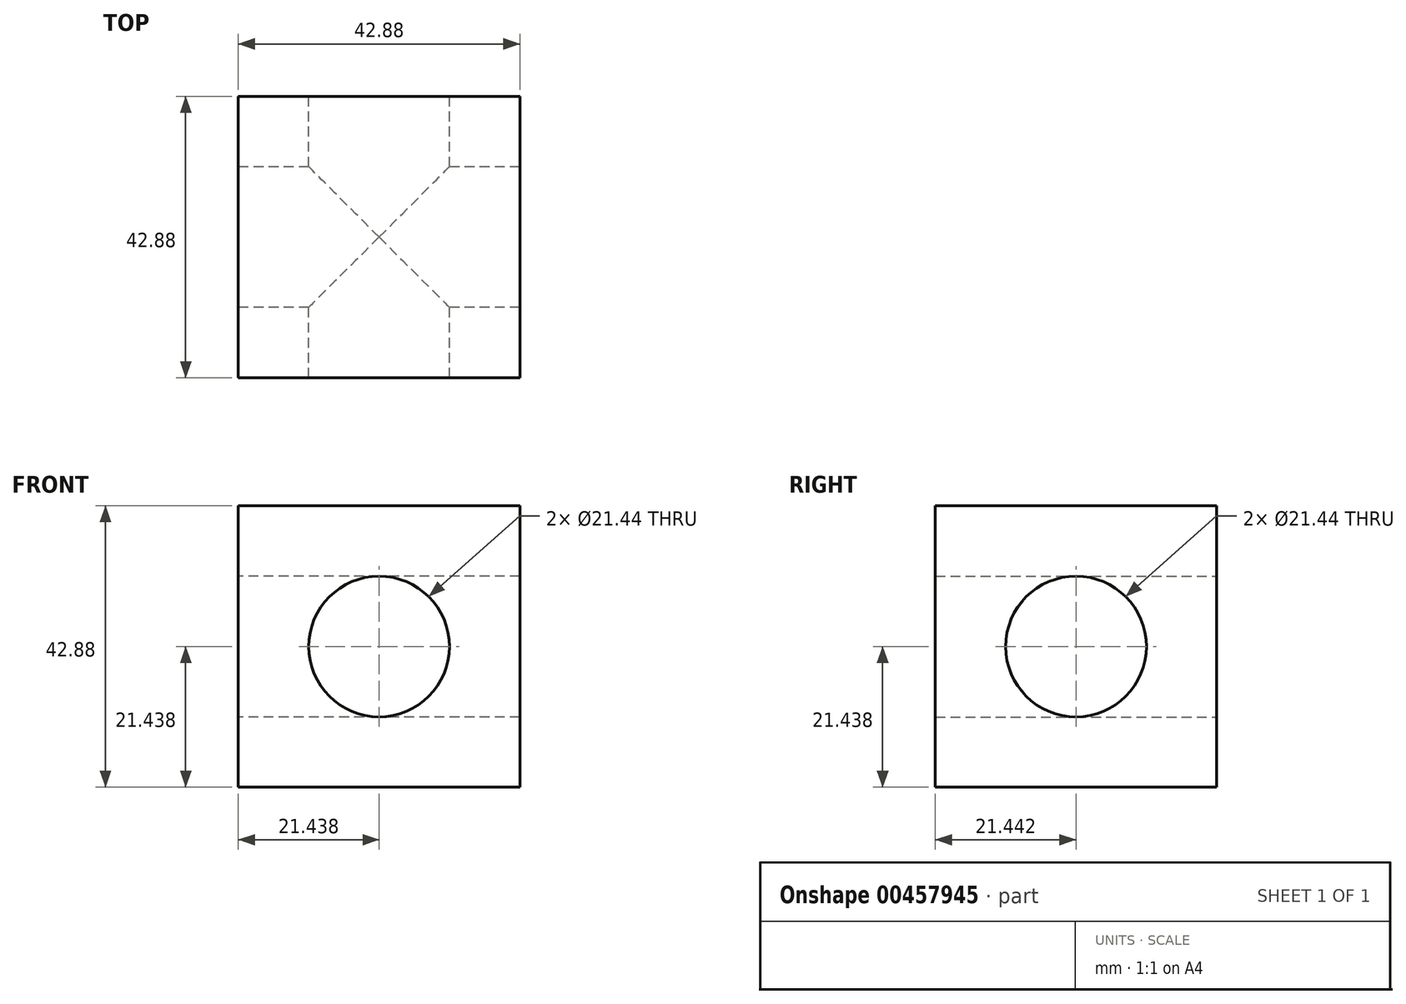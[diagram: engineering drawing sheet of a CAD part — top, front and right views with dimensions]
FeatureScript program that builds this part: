
annotation { "Feature Type Name" : "Feature", "Feature Type Description" : "" }
export const myFeature = defineFeature(function(context is Context, id is Id, definition is map)
    precondition{}
    {
        {
            var Q0;
            Q0=qCreatedBy(makeId("Front.planeOp"),FACE);
            var sketch = newSketch(context, id + "F0", { "sketchPlane" : qUnion([Q0])});
            skLineSegment(sketch, "E0.bottom", {"start": v(0, 0) * mm, "end": v(42.88, 0) * mm});
            skLineSegment(sketch, "E0.top", {"start": v(0, 42.88) * mm, "end": v(42.88, 42.88) * mm});
            skLineSegment(sketch, "E0.left", {"start": v(0, 0) * mm, "end": v(0, 42.88) * mm});
            skLineSegment(sketch, "E0.right", {"start": v(42.88, 0) * mm, "end": v(42.88, 42.88) * mm});
            skCircle(sketch, "E1", {"center": v(21.44, 21.44) * mm, "radius": 10.72 * mm});
            skSolve(sketch);
        }
        {
            var Q0;
            Q0=makeQuery(id+"F0.imprint","IMPRINT",FACE,{"disambiguationData":[TD([[makeQuery(id+"F0.imprint","IMPRINT",EDGE,{"derivedFrom":sQuery(id+"F0.wireOp",EDGE,"E0.bottom")}),1.0]])]});
            extrude(context, id + "F1", {"entities" : qUnion([Q0]), "depth" : 42.88 * mm, "offsetDistance" : 25.4 * mm});
        }
        {
            var Q0;
            Q0=makeQuery(id+"F1.opExtrude","SWEPT_FACE",FACE,{"disambiguationData":[OSD([sQuery(id+"F0.wireOp",EDGE,"E0.left")])]});
            var sketch = newSketch(context, id + "F2", { "sketchPlane" : qUnion([Q0])});
            skCircle(sketch, "E2", {"center": v(21.44, 21.44) * mm, "radius": 10.72 * mm});
            skSolve(sketch);
        }
        {
            var Q0;
            Q0=makeQuery(id+"F2.imprint","IMPRINT",FACE,{"disambiguationData":[TD([[makeQuery(id+"F2.imprint","IMPRINT",EDGE,{"derivedFrom":sQuery(id+"F2.wireOp",EDGE,"E2")}),1.0]])]});
            var Q1;
            Q1=makeQuery(id+"F1.opExtrude","SWEPT_FACE",FACE,{"disambiguationData":[OSD([sQuery(id+"F0.wireOp",EDGE,"E0.right")])]});
            extrude(context, id + "F3", {"entities" : qUnion([Q0, Q1]), "operationType" : NewBodyOperationType.REMOVE, "endBound" : BoundingType.THROUGH_ALL, "oppositeDirection" : true, "depth" : 66.8 * mm});
        }
    });
